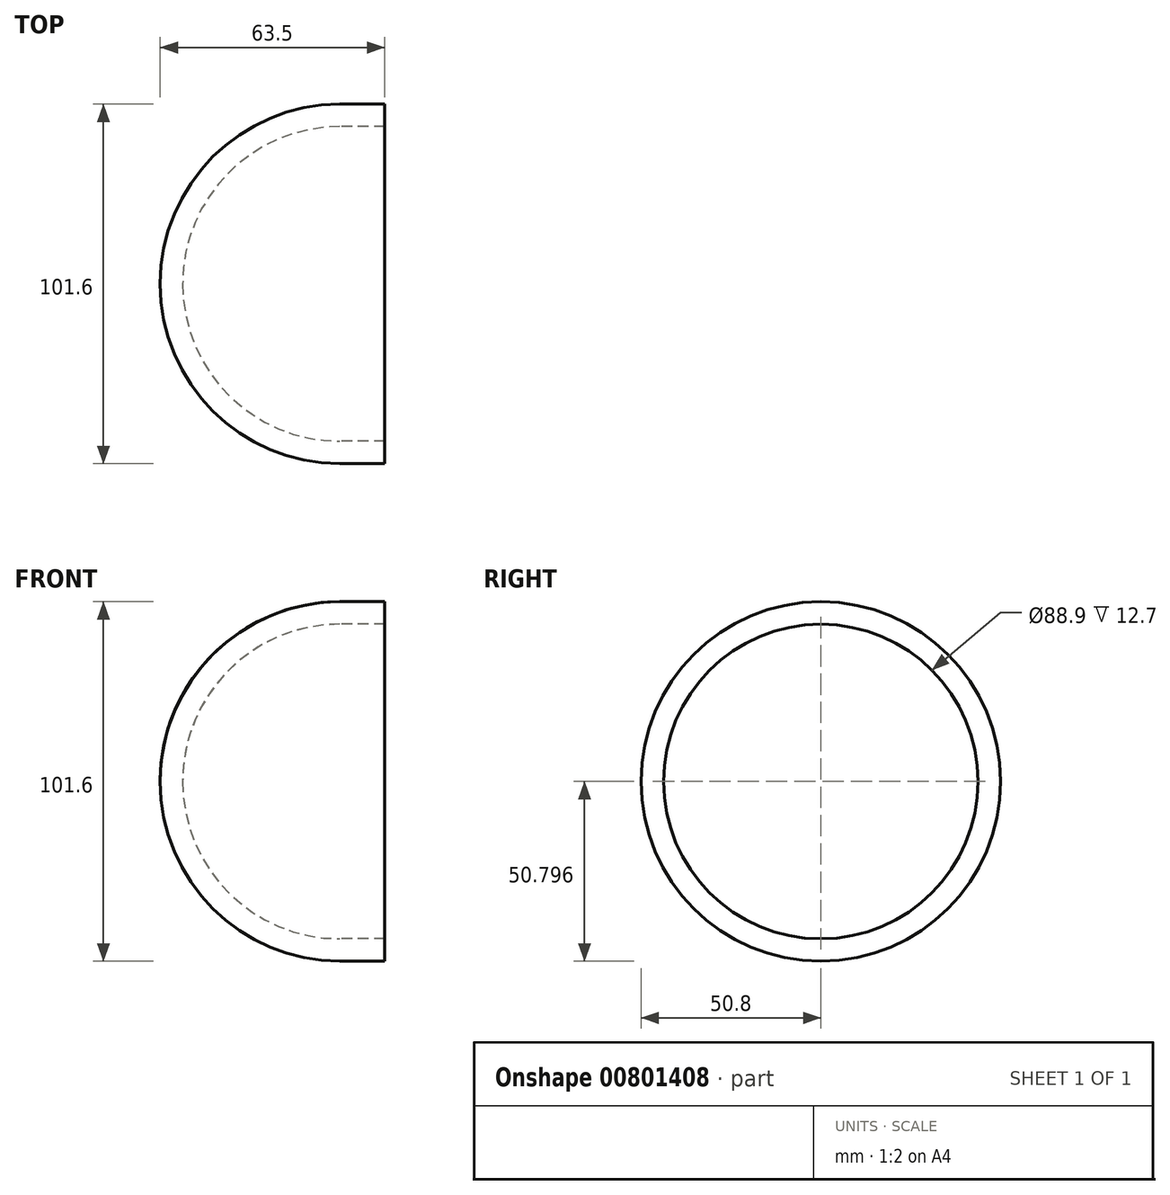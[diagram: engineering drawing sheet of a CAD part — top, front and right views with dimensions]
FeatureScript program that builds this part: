
annotation { "Feature Type Name" : "Feature", "Feature Type Description" : "" }
export const myFeature = defineFeature(function(context is Context, id is Id, definition is map)
    precondition{}
    {
        {
            var Q0;
            Q0=qCreatedBy(makeId("Front.planeOp"),FACE);
            var sketch = newSketch(context, id + "F0", { "sketchPlane" : qUnion([Q0])});
            skLineSegment(sketch, "E0", {"start": v(-71.74, 97.62) * mm, "end": v(-84.44, 97.62) * mm});
            skArc(sketch, "E1", {"start": v(-84.44, 97.62) * mm, "mid": v(-135.24, 46.82) * mm, "end": v(-84.44, -3.98) * mm});
            skLineSegment(sketch, "E2", {"start": v(-84.44, -3.98) * mm, "end": v(-71.74, -3.98) * mm});
            skLineSegment(sketch, "E3", {"start": v(-71.74, -3.98) * mm, "end": v(-71.74, 97.62) * mm});
            skLineSegment(sketch, "E4", {"start": v(-135.24, 46.82) * mm, "end": v(-71.74, 46.82) * mm});
            skSolve(sketch);
        }
        {
            var Q0;
            {var subQ0=sQuery(id+"F0.wireOp",EDGE,"E0");Q0=makeQuery(id+"F0.imprint","IMPRINT",FACE,{"disambiguationData":[TD([[makeQuery(id+"F0.imprint","IMPRINT",EDGE,{"derivedFrom":subQ0}),1.0]])]});}
            var Q1;
            Q1=sQuery(id+"F0.wireOp",EDGE,"E4");
            revolve(context, id + "F1", {"surfaceOperationType" : NewSurfaceOperationType.NEW, "entities" : qUnion([Q0]), "axis" : qUnion([Q1]), "revolveType" : RevolveType.FULL});
        }
        {
            var Q0;
            Q0=makeQuery(id+"F1.opRevolve","SWEPT_FACE",FACE,{"disambiguationData":[OSD([sQuery(id+"F0.wireOp",EDGE,"E3")])]});
            shell(context, id + "F2", {"entities" : qUnion([Q0]), "thickness" : 6.35 * mm});
        }
    });
